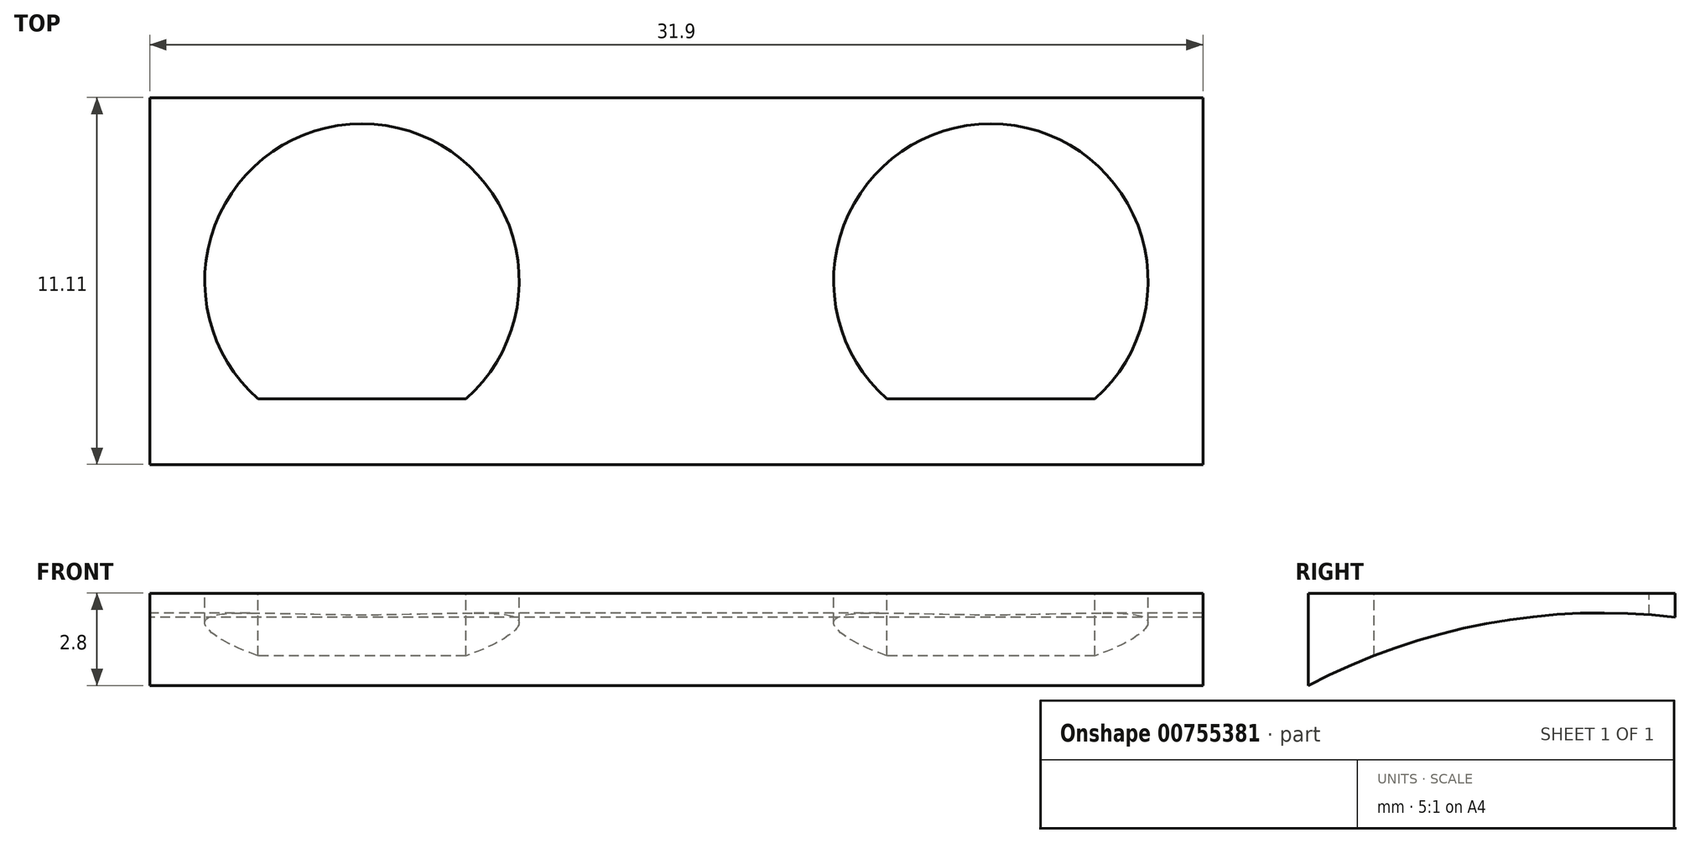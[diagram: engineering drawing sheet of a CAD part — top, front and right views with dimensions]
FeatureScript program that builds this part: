
annotation { "Feature Type Name" : "Feature", "Feature Type Description" : "" }
export const myFeature = defineFeature(function(context is Context, id is Id, definition is map)
    precondition{}
    {
        {
            var Q0;
            Q0=qCreatedBy(makeId("Right.planeOp"),FACE);
            var sketch = newSketch(context, id + "F0", { "sketchPlane" : qUnion([Q0])});
            skLineSegment(sketch, "E0.bottom", {"start": v(7.54, 0) * mm, "end": v(-7.54, 0) * mm, "construction": true});
            skPoint(sketch, "E0.middle", {"position": v(0, 0) * mm});
            skLineSegment(sketch, "E1", {"start": v(1.98, 1.59) * mm, "end": v(1.98, 0) * mm, "construction": true});
            skCircle(sketch, "E2", {"center": v(0, -15.87) * mm, "radius": 17.57 * mm, "construction": true});
            skCircle(sketch, "E3", {"center": v(0, -15.87) * mm, "radius": 19.16 * mm, "construction": true});
            skSolve(sketch);
        }
        {
            var Q0;
            Q0=qCreatedBy(makeId("Right.planeOp"),FACE);
            var sketch = newSketch(context, id + "F1", { "sketchPlane" : qUnion([Q0])});
            skLineSegment(sketch, "E4.0", {"start": v(7.54, 0) * mm, "end": v(-7.54, 0) * mm, "construction": true});
            skPoint(sketch, "E5.0", {"position": v(1.98, 0) * mm});
            skLineSegment(sketch, "E6", {"start": v(1.98, 0) * mm, "end": v(1.98, 1.6) * mm, "construction": true});
            skCircle(sketch, "E7", {"center": v(0, -15.75) * mm, "radius": 17.46 * mm, "construction": true});
            skCircle(sketch, "E8", {"center": v(0, -15.75) * mm, "radius": 19.05 * mm, "construction": true});
            skSolve(sketch);
        }
        {
            var Q0;
            Q0=qCreatedBy(makeId("Right.planeOp"),FACE);
            var sketch = newSketch(context, id + "F2", { "sketchPlane" : qUnion([Q0])});
            skLineSegment(sketch, "E9.bottom", {"start": v(-8.1, 16.34) * mm, "end": v(1.42, 16.34) * mm, "construction": true});
            skLineSegment(sketch, "E9.top", {"start": v(-8.1, -5.3) * mm, "end": v(1.42, -5.3) * mm, "construction": true});
            skLineSegment(sketch, "E9.left", {"start": v(-8.1, 16.34) * mm, "end": v(-8.1, -5.3) * mm, "construction": true});
            skLineSegment(sketch, "E9.right", {"start": v(1.42, 16.34) * mm, "end": v(1.42, -5.3) * mm, "construction": true});
            skLineSegment(sketch, "E10", {"start": v(-6.91, 16.34) * mm, "end": v(-6.91, -5.3) * mm, "construction": true});
            skLineSegment(sketch, "E11", {"start": v(3.01, 19.65) * mm, "end": v(3.01, -7.83) * mm, "construction": true});
            skLineSegment(sketch, "E12", {"start": v(3.01, -6.38) * mm, "end": v(-14, -6.38) * mm});
            skLineSegment(sketch, "E13", {"start": v(-14, -6.38) * mm, "end": v(3.01, -6.38) * mm});
            skCircle(sketch, "E14.0", {"center": v(0, -15.75) * mm, "radius": 17.46 * mm, "construction": true});
            skLineSegment(sketch, "E15", {"start": v(3.01, 1.45) * mm, "end": v(3.01, -6.38) * mm});
            skLineSegment(sketch, "E16", {"start": v(-14, -6.38) * mm, "end": v(-14, -5.32) * mm});
            skArc(sketch, "E17", {"start": v(-14, -5.32) * mm, "mid": v(-6.46, 0.47) * mm, "end": v(3.01, 1.45) * mm});
            skLineSegment(sketch, "E18", {"start": v(-8.9, 1.1) * mm, "end": v(-8.9, 3.9) * mm});
            skLineSegment(sketch, "E19", {"start": v(-8.9, 3.9) * mm, "end": v(2.22, 3.9) * mm});
            skLineSegment(sketch, "E20", {"start": v(2.22, 3.9) * mm, "end": v(2.22, 3.17) * mm});
            skArc(sketch, "E21", {"start": v(-8.9, 1.1) * mm, "mid": v(-3.5, 2.98) * mm, "end": v(2.22, 3.17) * mm});
            skPoint(sketch, "E22", {"position": v(-3.34, 16.34) * mm});
            skPoint(sketch, "E23", {"position": v(-3.34, 3.9) * mm});
            skSolve(sketch);
        }
        {
            var Q0;
            Q0=qCreatedBy(makeId("Top.planeOp"),FACE);
            var sketch = newSketch(context, id + "F3", { "sketchPlane" : qUnion([Q0])});
            skLineSegment(sketch, "E24.bottom", {"start": v(-15.95, -14) * mm, "end": v(15.95, -14) * mm});
            skLineSegment(sketch, "E24.top", {"start": v(-15.95, 3.01) * mm, "end": v(15.95, 3.01) * mm});
            skLineSegment(sketch, "E24.left", {"start": v(-15.95, -14) * mm, "end": v(-15.95, 3.01) * mm});
            skLineSegment(sketch, "E24.right", {"start": v(15.95, -14) * mm, "end": v(15.95, 3.01) * mm});
            skPoint(sketch, "E24.middle", {"position": v(0, -5.5) * mm});
            skPoint(sketch, "E25.0", {"position": v(0, -14) * mm});
            skPoint(sketch, "E26.0", {"position": v(0, 3.01) * mm});
            skLineSegment(sketch, "E27", {"start": v(-9.53, -3.34) * mm, "end": v(9.53, -3.34) * mm, "construction": true});
            skCircle(sketch, "E28", {"center": v(-9.53, -3.34) * mm, "radius": 4.76 * mm, "construction": true});
            skCircle(sketch, "E29", {"center": v(9.53, -3.34) * mm, "radius": 4.76 * mm, "construction": true});
            skPoint(sketch, "E30.0", {"position": v(0, -6.91) * mm});
            skLineSegment(sketch, "E31", {"start": v(-12.68, -6.91) * mm, "end": v(12.68, -6.91) * mm, "construction": true});
            skLineSegment(sketch, "E32", {"start": v(-12.68, -6.91) * mm, "end": v(-6.37, -6.91) * mm});
            skLineSegment(sketch, "E33", {"start": v(12.68, -6.91) * mm, "end": v(6.37, -6.91) * mm});
            skArc(sketch, "E34", {"start": v(-12.68, -6.91) * mm, "mid": v(-9.53, 1.42) * mm, "end": v(-6.37, -6.91) * mm});
            skArc(sketch, "E35", {"start": v(6.37, -6.91) * mm, "mid": v(9.52, 1.42) * mm, "end": v(12.68, -6.91) * mm});
            skPoint(sketch, "E36.0", {"position": v(0, 1.42) * mm});
            skPoint(sketch, "E37.0", {"position": v(0, -8.1) * mm});
            skLineSegment(sketch, "E38", {"start": v(0, 1.42) * mm, "end": v(0, -8.1) * mm, "construction": true});
            skPoint(sketch, "E39", {"position": v(0, -3.34) * mm});
            skSolve(sketch);
        }
        {
            var Q0;
            Q0=makeQuery(id+"F2.imprint","IMPRINT",FACE,{"disambiguationData":[TD([[makeQuery(id+"F2.imprint","IMPRINT",EDGE,{"derivedFrom":sQuery(id+"F2.wireOp",EDGE,"E13")}),1.0]])]});
            var Q1;
            Q1=makeQuery(id+"F2.imprint","IMPRINT",FACE,{"disambiguationData":[TD([[makeQuery(id+"F2.imprint","IMPRINT",EDGE,{"derivedFrom":sQuery(id+"F2.wireOp",EDGE,"E18")}),-1.0]])]});
            var Q2;
            Q2=sQuery(id+"F3.wireOp",VERTEX,"E24.bottom.end");
            var Q3;
            Q3=sQuery(id+"F3.wireOp",VERTEX,"E24.left.start");
            extrude(context, id + "F4", {"entities" : qUnion([Q0, Q1]), "endBound" : BoundingType.UP_TO_VERTEX, "depth" : 25.4 * mm, "endBoundEntityVertex" : qUnion([Q2]), "offsetDistance" : 25.4 * mm, "hasSecondDirection" : true, "secondDirectionBound" : SecondDirectionBoundingType.UP_TO_VERTEX, "secondDirectionOppositeDirection" : true, "secondDirectionDepth" : 25.4 * mm, "secondDirectionBoundEntityVertex" : qUnion([Q3])});
        }
        {
            var Q0;
            Q0=makeQuery(id+"F3.imprint","IMPRINT",FACE,{"disambiguationData":[TD([[makeQuery(id+"F3.imprint","IMPRINT",EDGE,{"derivedFrom":sQuery(id+"F3.wireOp",EDGE,"E32")}),1.0]])]});
            var Q1;
            Q1=makeQuery(id+"F3.imprint","IMPRINT",FACE,{"disambiguationData":[TD([[makeQuery(id+"F3.imprint","IMPRINT",EDGE,{"derivedFrom":sQuery(id+"F3.wireOp",EDGE,"E33")}),-1.0]])]});
            extrude(context, id + "F5", {"entities" : qUnion([Q0, Q1]), "operationType" : NewBodyOperationType.REMOVE, "endBound" : BoundingType.THROUGH_ALL, "oppositeDirection" : true, "depth" : 25.4 * mm, "offsetDistance" : 25.4 * mm, "hasSecondDirection" : true, "secondDirectionBound" : SecondDirectionBoundingType.THROUGH_ALL, "secondDirectionOppositeDirection" : false, "secondDirectionDepth" : 25.4 * mm});
        }
    });
